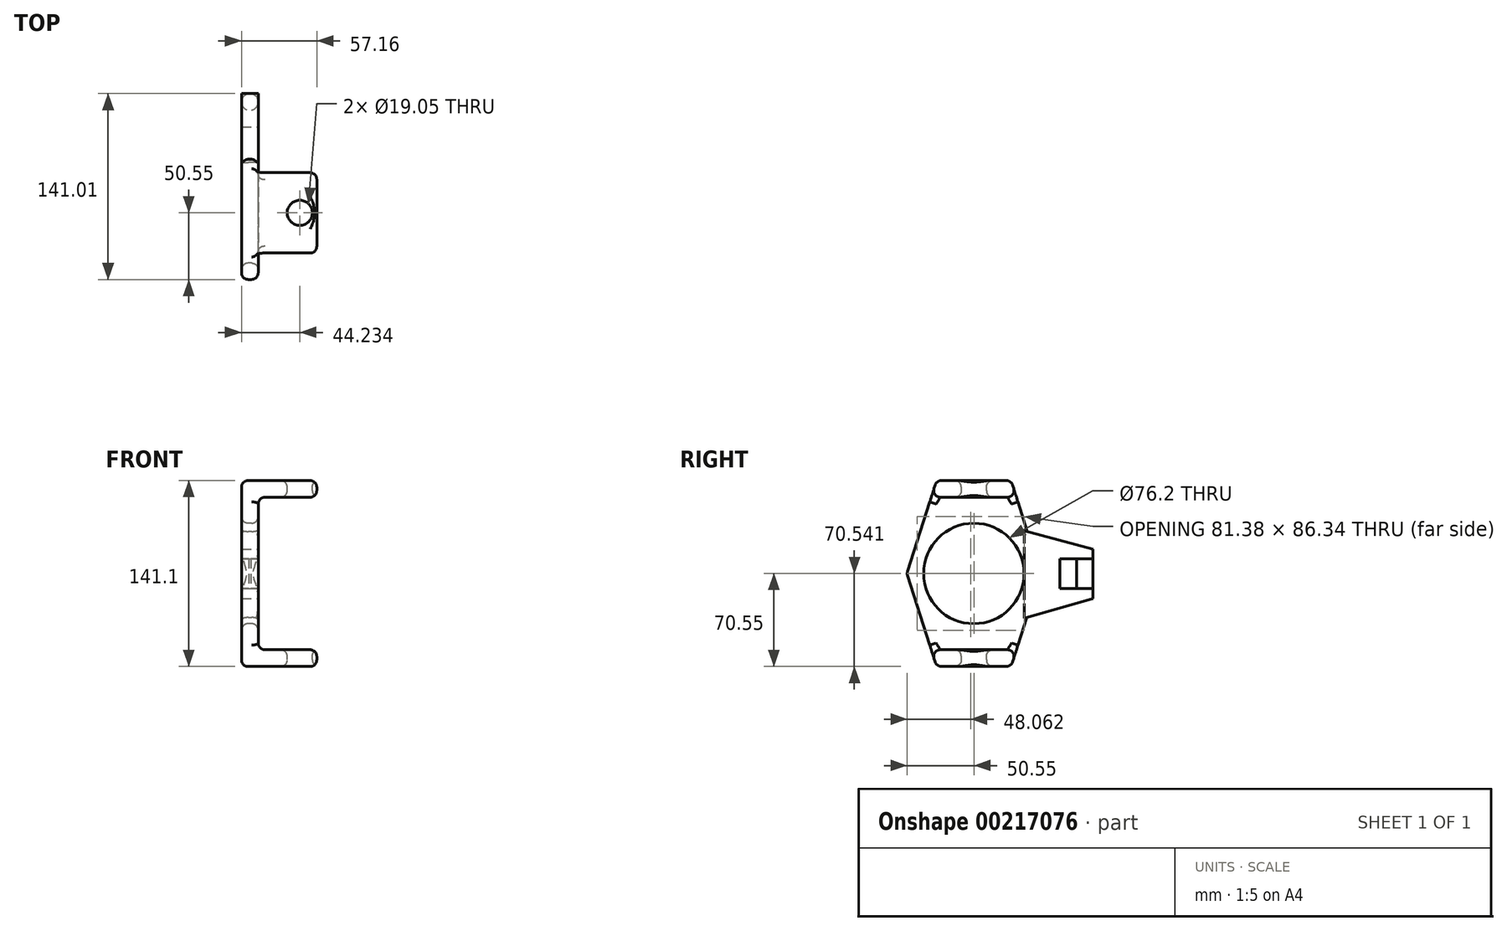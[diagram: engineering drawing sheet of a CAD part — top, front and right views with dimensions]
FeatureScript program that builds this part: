
annotation { "Feature Type Name" : "Feature", "Feature Type Description" : "" }
export const myFeature = defineFeature(function(context is Context, id is Id, definition is map)
    precondition{}
    {
        {
            var Q0;
            Q0=qCreatedBy(makeId("Front.planeOp"),FACE);
            var sketch = newSketch(context, id + "F0", { "sketchPlane" : qUnion([Q0])});
            skLineSegment(sketch, "E0.bottom", {"start": v(22.22, 57.85) * mm, "end": v(-22.23, 57.85) * mm});
            skLineSegment(sketch, "E0.top", {"start": v(22.22, -57.85) * mm, "end": v(-22.23, -57.85) * mm});
            skLineSegment(sketch, "E0.right", {"start": v(-22.23, 57.85) * mm, "end": v(-22.23, -57.85) * mm});
            skPoint(sketch, "E0.middle", {"position": v(0, 0) * mm});
            skLineSegment(sketch, "E1.0", {"start": v(22.22, -70.55) * mm, "end": v(-34.93, -70.55) * mm});
            skLineSegment(sketch, "E1.1", {"start": v(-34.93, 70.55) * mm, "end": v(-34.93, -70.55) * mm});
            skLineSegment(sketch, "E1.2", {"start": v(22.22, 70.55) * mm, "end": v(-34.93, 70.55) * mm});
            skLineSegment(sketch, "E2", {"start": v(22.22, 70.55) * mm, "end": v(22.22, 57.85) * mm});
            skLineSegment(sketch, "E3", {"start": v(22.22, -57.85) * mm, "end": v(22.22, -70.55) * mm});
            skSolve(sketch);
        }
        {
            var Q0;
            Q0=makeQuery(id+"F0.imprint","IMPRINT",FACE,{"disambiguationData":[TD([[makeQuery(id+"F0.imprint","IMPRINT",EDGE,{"derivedFrom":sQuery(id+"F0.wireOp",EDGE,"E0.bottom")}),-1.0]])]});
            extrude(context, id + "F1", {"entities" : qUnion([Q0]), "depth" : 101.6 * mm});
        }
        {
            var Q0;
            Q0=makeQuery(id+"F1.opExtrude","SWEPT_FACE",FACE,{"disambiguationData":[OSD([sQuery(id+"F0.wireOp",EDGE,"E1.1")])]});
            var sketch = newSketch(context, id + "F2", { "sketchPlane" : qUnion([Q0])});
            skCircle(sketch, "E4", {"center": v(50.8, 0) * mm, "radius": 38.1 * mm});
            skPoint(sketch, "E4.centerSnap0", {"position": v(50.8, -70.55) * mm});
            skLineSegment(sketch, "E5.bottom", {"start": v(79.08, -70.55) * mm, "end": v(22.52, -70.55) * mm, "construction": true});
            skLineSegment(sketch, "E5.top", {"start": v(79.08, 70.55) * mm, "end": v(22.52, 70.55) * mm, "construction": true});
            skLineSegment(sketch, "E5.left", {"start": v(79.08, -70.55) * mm, "end": v(79.08, 70.55) * mm, "construction": true});
            skLineSegment(sketch, "E5.right", {"start": v(22.52, -70.55) * mm, "end": v(22.52, 70.55) * mm, "construction": true});
            skLineSegment(sketch, "E6", {"start": v(79.08, -70.55) * mm, "end": v(101.6, 0) * mm});
            skLineSegment(sketch, "E7", {"start": v(101.6, 0) * mm, "end": v(79.08, 70.55) * mm});
            skLineSegment(sketch, "E8", {"start": v(22.52, 70.55) * mm, "end": v(0, 0) * mm});
            skLineSegment(sketch, "E9", {"start": v(0, 0) * mm, "end": v(22.52, -70.55) * mm});
            skSolve(sketch);
        }
        {
            var Q0;
            {var subQ0=sQuery(id+"F2.wireOp",EDGE,"E9");Q0=makeQuery(id+"F2.imprint","IMPRINT",FACE,{"disambiguationData":[TD([[makeQuery(id+"F2.imprint","IMPRINT",EDGE,{"derivedFrom":subQ0}),-1.0]])]});}
            var Q1;
            {var subQ0=sQuery(id+"F2.wireOp",EDGE,"E8");Q1=makeQuery(id+"F2.imprint","IMPRINT",FACE,{"disambiguationData":[TD([[makeQuery(id+"F2.imprint","IMPRINT",EDGE,{"derivedFrom":subQ0}),-1.0]])]});}
            var Q2;
            {var subQ0=sQuery(id+"F2.wireOp",EDGE,"E7");Q2=makeQuery(id+"F2.imprint","IMPRINT",FACE,{"disambiguationData":[TD([[makeQuery(id+"F2.imprint","IMPRINT",EDGE,{"derivedFrom":subQ0}),-1.0]])]});}
            var Q3;
            {var subQ0=sQuery(id+"F2.wireOp",EDGE,"E6");Q3=makeQuery(id+"F2.imprint","IMPRINT",FACE,{"disambiguationData":[TD([[makeQuery(id+"F2.imprint","IMPRINT",EDGE,{"derivedFrom":subQ0}),-1.0]])]});}
            var Q4;
            Q4=makeQuery(id+"F2.imprint","IMPRINT",FACE,{"disambiguationData":[TD([[makeQuery(id+"F2.imprint","IMPRINT",EDGE,{"derivedFrom":sQuery(id+"F2.wireOp",EDGE,"E4")}),1.0]])]});
            extrude(context, id + "F3", {"entities" : qUnion([Q0, Q1, Q2, Q3, Q4]), "operationType" : NewBodyOperationType.REMOVE, "endBound" : BoundingType.THROUGH_ALL, "oppositeDirection" : true, "depth" : 25.4 * mm});
        }
        {
            var Q0;
            Q0=makeQuery(id+"F1.opExtrude","SWEPT_FACE",FACE,{"disambiguationData":[OSD([sQuery(id+"F0.wireOp",EDGE,"E1.2")])]});
            var sketch = newSketch(context, id + "F4", { "sketchPlane" : qUnion([Q0])});
            skCircle(sketch, "E10", {"center": v(9.3, -50.8) * mm, "radius": 9.53 * mm});
            skPoint(sketch, "E10.centerSnap0", {"position": v(22.22, -50.8) * mm});
            skSolve(sketch);
        }
        {
            var Q0;
            Q0=makeQuery(id+"F4.imprint","IMPRINT",FACE,{"disambiguationData":[TD([[makeQuery(id+"F4.imprint","IMPRINT",EDGE,{"derivedFrom":sQuery(id+"F4.wireOp",EDGE,"E10")}),1.0]])]});
            extrude(context, id + "F5", {"entities" : qUnion([Q0]), "operationType" : NewBodyOperationType.REMOVE, "endBound" : BoundingType.THROUGH_ALL, "oppositeDirection" : true, "depth" : 25.4 * mm});
        }
        {
            var Q0;
            Q0=makeQuery(id+"F3.boolean.opBoolean","COPY",EDGE,{"derivedFrom":makeQuery(id+"F3.opExtrude","SWEPT_EDGE",EDGE,{"disambiguationData":[OSD([sQuery(id+"F0.wireOp",EDGE,"E1.1"),sQuery(id+"F0.wireOp",EDGE,"E1.2"),sQuery(id+"F2.wireOp",EDGE,"E8")])]})});
            var Q1;
            Q1=makeQuery(id+"F1.opExtrude","SWEPT_EDGE",EDGE,{"disambiguationData":[OSD([sQuery(id+"F0.wireOp",EDGE,"E1.1"),sQuery(id+"F0.wireOp",EDGE,"E1.2")])]});
            var Q2;
            Q2=makeQuery(id+"F3.boolean.opBoolean","COPY",EDGE,{"derivedFrom":makeQuery(id+"F3.opExtrude","SWEPT_EDGE",EDGE,{"disambiguationData":[OSD([sQuery(id+"F0.wireOp",EDGE,"E1.1"),sQuery(id+"F0.wireOp",EDGE,"E1.2"),sQuery(id+"F2.wireOp",EDGE,"E7")])]})});
            var Q3;
            Q3=makeQuery(id+"F1.opExtrude","SWEPT_EDGE",EDGE,{"disambiguationData":[OSD([sQuery(id+"F0.wireOp",EDGE,"E1.2"),sQuery(id+"F0.wireOp",EDGE,"E2")])]});
            var Q4;
            Q4=makeQuery(id+"F1.opExtrude","SWEPT_FACE",FACE,{"disambiguationData":[OSD([sQuery(id+"F0.wireOp",EDGE,"E1.1")])]});
            var Q5;
            Q5=makeQuery(id+"F3.boolean.opBoolean","COPY",FACE,{"derivedFrom":makeQuery(id+"F3.opExtrude","SWEPT_FACE",FACE,{"disambiguationData":[OSD([sQuery(id+"F2.wireOp",EDGE,"E8")])]})});
            var Q6;
            Q6=makeQuery(id+"F3.boolean.opBoolean","COPY",FACE,{"derivedFrom":makeQuery(id+"F3.opExtrude","SWEPT_FACE",FACE,{"disambiguationData":[OSD([sQuery(id+"F2.wireOp",EDGE,"E9")])]})});
            var Q7;
            Q7=makeQuery(id+"F1.opExtrude","SWEPT_FACE",FACE,{"disambiguationData":[OSD([sQuery(id+"F0.wireOp",EDGE,"E1.0")])]});
            var Q8;
            Q8=makeQuery(id+"F3.boolean.opBoolean","COPY",FACE,{"derivedFrom":makeQuery(id+"F3.opExtrude","SWEPT_FACE",FACE,{"disambiguationData":[OSD([sQuery(id+"F2.wireOp",EDGE,"E6")])]})});
            var Q9;
            Q9=makeQuery(id+"F3.boolean.opBoolean","COPY",FACE,{"derivedFrom":makeQuery(id+"F3.opExtrude","SWEPT_FACE",FACE,{"disambiguationData":[OSD([sQuery(id+"F2.wireOp",EDGE,"E7")])]})});
            var Q10;
            Q10=makeQuery(id+"F1.opExtrude","SWEPT_FACE",FACE,{"disambiguationData":[OSD([sQuery(id+"F0.wireOp",EDGE,"E0.bottom")])]});
            var Q11;
            Q11=makeQuery(id+"F1.opExtrude","SWEPT_FACE",FACE,{"disambiguationData":[OSD([sQuery(id+"F0.wireOp",EDGE,"E0.top")])]});
            var Q12;
            Q12=makeQuery(id+"F1.opExtrude","SWEPT_FACE",FACE,{"disambiguationData":[OSD([sQuery(id+"F0.wireOp",EDGE,"E1.2")])]});
            var Q13;
            Q13=makeQuery(id+"F3.boolean.opBoolean","INTERSECT",EDGE,{"derivedFrom":[makeQuery(id+"F1.opExtrude","SWEPT_FACE",FACE,{"disambiguationData":[OSD([sQuery(id+"F0.wireOp",EDGE,"E0.right")])]}),makeQuery(id+"F3.opExtrude","SWEPT_FACE",FACE,{"disambiguationData":[OSD([sQuery(id+"F2.wireOp",EDGE,"E4")])]})]});
            fillet(context, id + "F6", {"entities" : qUnion([Q0, Q1, Q2, Q3, Q4, Q5, Q6, Q7, Q8, Q9, Q10, Q11, Q12, Q13]), "radius" : 5.08 * mm, "tangentPropagation" : true, "allowEdgeOverflow" : false});
        }
        {
            var Q0;
            Q0=qCreatedBy(makeId("Right.planeOp"),FACE);
            var sketch = newSketch(context, id + "F7", { "sketchPlane" : qUnion([Q0])});
            skLineSegment(sketch, "E11.left", {"start": v(-12.6, 32.52) * mm, "end": v(-12.6, -33.96) * mm});
            skLineSegment(sketch, "E12.right", {"start": v(-12.6, -11.3) * mm, "end": v(-12.6, 11.3) * mm, "construction": true});
            skPoint(sketch, "E12.middle", {"position": v(27.22, 0) * mm});
            skPoint(sketch, "E12.middle.positionSnap0", {"position": v(27.22, 32.52) * mm});
            skPoint(sketch, "E12.centerSnap0", {"position": v(27.22, 32.52) * mm});
            skLineSegment(sketch, "E13", {"start": v(-12.6, 32.52) * mm, "end": v(39.66, 18.6) * mm});
            skLineSegment(sketch, "E14", {"start": v(39.66, -19.09) * mm, "end": v(-12.6, -33.96) * mm});
            skLineSegment(sketch, "E15", {"start": v(39.66, 18.6) * mm, "end": v(39.66, 11.3) * mm});
            skLineSegment(sketch, "E16.trimOffspring", {"start": v(39.66, -11.3) * mm, "end": v(39.66, -19.09) * mm});
            skLineSegment(sketch, "E17", {"start": v(39.66, -19.09) * mm, "end": v(39.66, -11.3) * mm});
            skLineSegment(sketch, "E18.bottom", {"start": v(39.66, -11.3) * mm, "end": v(14.3, -11.3) * mm});
            skLineSegment(sketch, "E18.top", {"start": v(39.66, 11.3) * mm, "end": v(14.3, 11.3) * mm});
            skLineSegment(sketch, "E18.right", {"start": v(14.3, -11.3) * mm, "end": v(14.3, 11.3) * mm});
            skPoint(sketch, "E19.orphan", {"position": v(39.66, -33.96) * mm});
            skPoint(sketch, "E20.start.orphan", {"position": v(67.05, -11.3) * mm});
            skPoint(sketch, "E11.right.end.orphan", {"position": v(67.05, 11.3) * mm});
            skPoint(sketch, "E11.bottom.end.orphan", {"position": v(67.05, 32.52) * mm});
            skLineSegment(sketch, "E21.trimOffspring", {"start": v(39.66, 11.3) * mm, "end": v(39.66, 18.6) * mm});
            skSolve(sketch);
        }
        {
            var Q0;
            Q0=makeQuery(id+"F7.imprint","IMPRINT",FACE,{"disambiguationData":[TD([[makeQuery(id+"F7.imprint","IMPRINT",EDGE,{"derivedFrom":sQuery(id+"F7.wireOp",EDGE,"E11.left")}),1.0]])]});
            var Q1;
            Q1=makeQuery(id+"F1.opExtrude","SWEPT_FACE",FACE,{"disambiguationData":[OSD([sQuery(id+"F0.wireOp",EDGE,"E0.right")])]});
            extrude(context, id + "F8", {"entities" : qUnion([Q0]), "operationType" : NewBodyOperationType.ADD, "oppositeDirection" : true, "depth" : 34.92 * mm, "hasSecondDirection" : true, "secondDirectionBound" : BoundingType.UP_TO_SURFACE, "secondDirectionOppositeDirection" : true, "secondDirectionBoundEntityFace" : qUnion([Q1]), "secondDirectionDepth" : 25.4 * mm});
        }
        {
            var Q0;
            Q0=makeQuery(id+"F8.opExtrude","SWEPT_FACE",FACE,{"disambiguationData":[OSD([sQuery(id+"F7.wireOp",EDGE,"E18.bottom")])]});
            var sketch = newSketch(context, id + "F9", { "sketchPlane" : qUnion([Q0])});
            skCircle(sketch, "E22", {"center": v(-28.58, 33.36) * mm, "radius": 6.35 * mm});
            skPoint(sketch, "E22.centerSnap0", {"position": v(-28.58, 39.66) * mm});
            skSolve(sketch);
        }
        {
            var Q0;
            {var subQ0=sQuery(id+"F9.wireOp",EDGE,"E22");var subQ1=sQuery(id+"F7.wireOp",EDGE,"E18.bottom");var subQ6=makeQuery(id+"F9.imprint","INTERSECT",VERTEX,{"derivedFrom":[makeQuery(id+"F8.opExtrude","CAP_EDGE",EDGE,{"disambiguationData":[OSD([subQ1])],"isStart":false}),subQ0]});Q0=makeQuery(id+"F9.imprint","IMPRINT",FACE,{"disambiguationData":[TD([[makeQuery(id+"F9.imprint","IMPRINT",EDGE,{"disambiguationData":[TD([[subQ6,1.0]])],"derivedFrom":subQ0}),1.0]])]});}
            var Q1;
            Q1=makeQuery(id+"F8.opExtrude","SWEPT_FACE",FACE,{"disambiguationData":[OSD([sQuery(id+"F7.wireOp",EDGE,"E18.top")])]});
            extrude(context, id + "F10", {"entities" : qUnion([Q0]), "operationType" : NewBodyOperationType.ADD, "endBound" : BoundingType.UP_TO_SURFACE, "endBoundEntityFace" : qUnion([Q1]), "depth" : 25.4 * mm});
        }
    });
